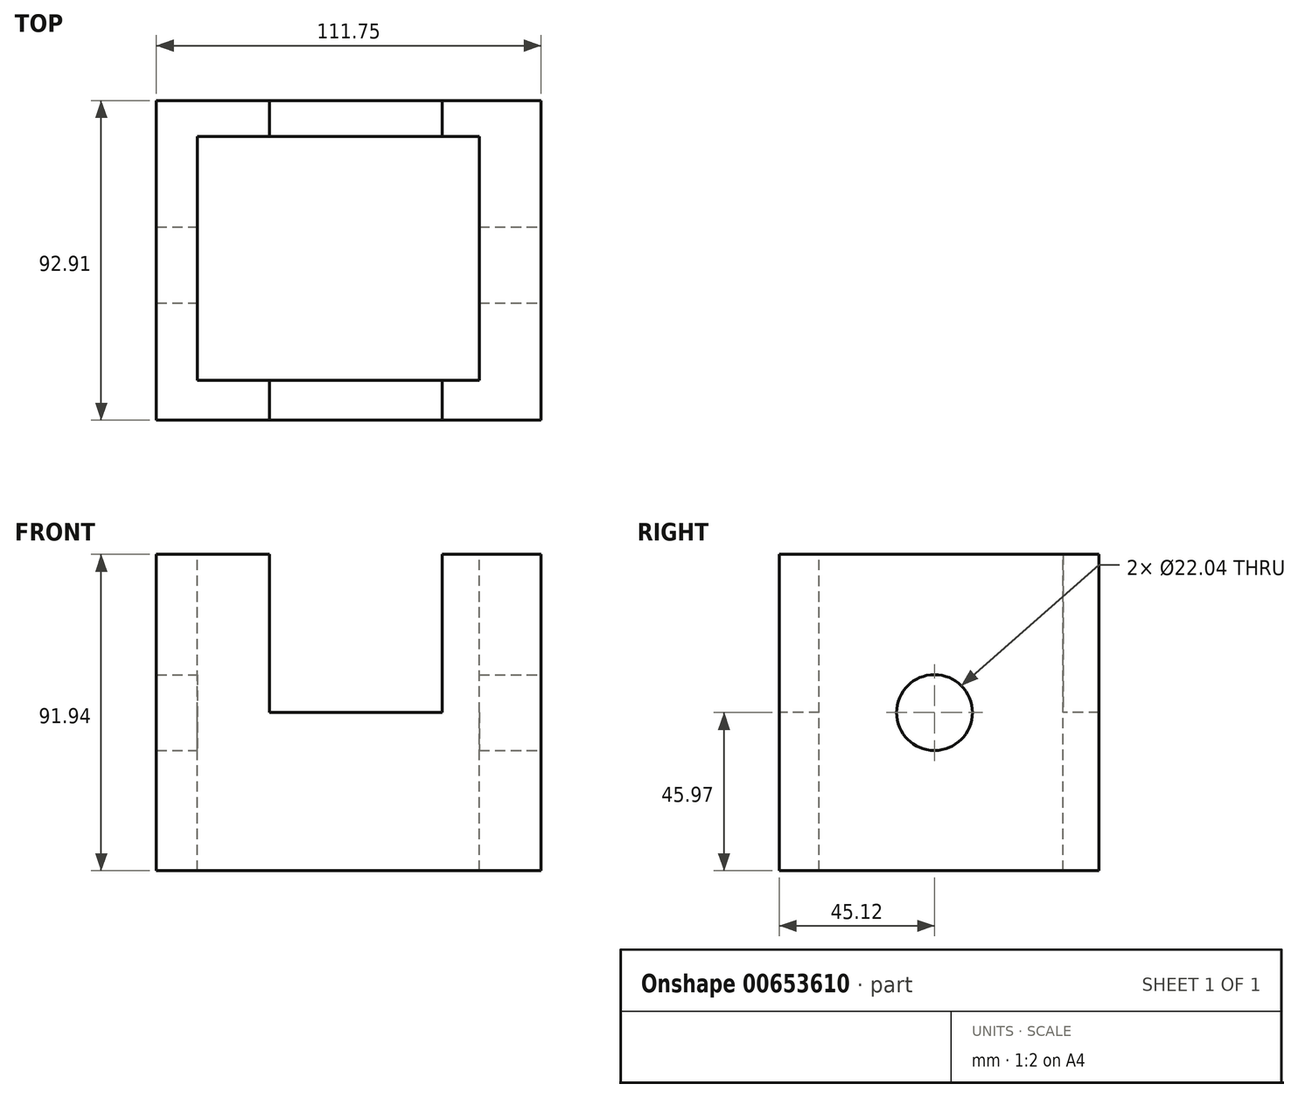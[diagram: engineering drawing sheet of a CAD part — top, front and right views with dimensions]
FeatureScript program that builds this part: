
annotation { "Feature Type Name" : "Feature", "Feature Type Description" : "" }
export const myFeature = defineFeature(function(context is Context, id is Id, definition is map)
    precondition{}
    {
        {
            var Q0;
            Q0=qCreatedBy(makeId("Top.planeOp"),FACE);
            var sketch = newSketch(context, id + "F0", { "sketchPlane" : qUnion([Q0])});
            skLineSegment(sketch, "E0", {"start": v(-56.34, 47.8) * mm, "end": v(-56.34, -45.12) * mm});
            skLineSegment(sketch, "E1", {"start": v(-56.34, -45.12) * mm, "end": v(55.41, -45.12) * mm});
            skLineSegment(sketch, "E2", {"start": v(55.41, -45.12) * mm, "end": v(55.41, 47.8) * mm});
            skLineSegment(sketch, "E3", {"start": v(55.41, 47.8) * mm, "end": v(-56.34, 47.8) * mm});
            skSolve(sketch);
        }
        {
            var Q0;
            Q0=makeQuery(id+"F0.imprint","IMPRINT",FACE,{"disambiguationData":[TD([[makeQuery(id+"F0.imprint","IMPRINT",EDGE,{"derivedFrom":sQuery(id+"F0.wireOp",EDGE,"E0")}),1.0]])]});
            extrude(context, id + "F1", {"entities" : qUnion([Q0]), "endBound" : BoundingType.SYMMETRIC, "depth" : 91.95 * mm, "offsetDistance" : 25.4 * mm});
        }
        {
            var Q0;
            Q0=makeQuery(id+"F1.opExtrude","CAP_FACE",FACE,{"disambiguationData":[OSD([sQuery(id+"F0.wireOp",EDGE,"E0"),sQuery(id+"F0.wireOp",EDGE,"E1"),sQuery(id+"F0.wireOp",EDGE,"E2"),sQuery(id+"F0.wireOp",EDGE,"E3")])],"isStart":false});
            var sketch = newSketch(context, id + "F2", { "sketchPlane" : qUnion([Q0])});
            skLineSegment(sketch, "E4", {"start": v(-44.43, 37.4) * mm, "end": v(37.4, 37.4) * mm});
            skLineSegment(sketch, "E5", {"start": v(37.4, 37.4) * mm, "end": v(37.4, -33.47) * mm});
            skLineSegment(sketch, "E6", {"start": v(37.4, -33.47) * mm, "end": v(-44.43, -33.47) * mm});
            skLineSegment(sketch, "E7", {"start": v(-44.43, -33.47) * mm, "end": v(-44.43, 37.4) * mm});
            skSolve(sketch);
        }
        {
            var Q0;
            Q0=makeQuery(id+"F2.imprint","IMPRINT",FACE,{"disambiguationData":[TD([[makeQuery(id+"F2.imprint","IMPRINT",EDGE,{"derivedFrom":sQuery(id+"F2.wireOp",EDGE,"E4")}),-1.0]])]});
            extrude(context, id + "F3", {"entities" : qUnion([Q0]), "operationType" : NewBodyOperationType.REMOVE, "endBound" : BoundingType.SYMMETRIC, "oppositeDirection" : true, "depth" : 219.46 * mm, "offsetDistance" : 25.4 * mm});
        }
        {
            var Q0;
            Q0=makeQuery(id+"F1.opExtrude","SWEPT_FACE",FACE,{"disambiguationData":[OSD([sQuery(id+"F0.wireOp",EDGE,"E2")])]});
            var sketch = newSketch(context, id + "F4", { "sketchPlane" : qUnion([Q0])});
            skCircle(sketch, "E8", {"center": v(0, 0) * mm, "radius": 11.02 * mm});
            skSolve(sketch);
        }
        {
            var Q0;
            Q0=makeQuery(id+"F4.imprint","IMPRINT",FACE,{"disambiguationData":[TD([[makeQuery(id+"F4.imprint","IMPRINT",EDGE,{"derivedFrom":sQuery(id+"F4.wireOp",EDGE,"E8")}),1.0]])]});
            extrude(context, id + "F5", {"entities" : qUnion([Q0]), "operationType" : NewBodyOperationType.REMOVE, "oppositeDirection" : true, "depth" : 176.02 * mm, "offsetDistance" : 25.4 * mm});
        }
        {
            var Q0;
            Q0=makeQuery(id+"F1.opExtrude","SWEPT_FACE",FACE,{"disambiguationData":[OSD([sQuery(id+"F0.wireOp",EDGE,"E1")])]});
            var sketch = newSketch(context, id + "F6", { "sketchPlane" : qUnion([Q0])});
            skLineSegment(sketch, "E9", {"start": v(-23.52, 45.97) * mm, "end": v(-23.52, 0) * mm});
            skLineSegment(sketch, "E10", {"start": v(-23.52, 0) * mm, "end": v(26.67, 0) * mm});
            skLineSegment(sketch, "E11", {"start": v(26.67, 0) * mm, "end": v(26.67, 45.97) * mm});
            skLineSegment(sketch, "E12", {"start": v(26.67, 45.97) * mm, "end": v(-23.52, 45.97) * mm});
            skSolve(sketch);
        }
        {
            var Q0;
            Q0=makeQuery(id+"F6.imprint","IMPRINT",FACE,{"disambiguationData":[TD([[makeQuery(id+"F6.imprint","IMPRINT",EDGE,{"derivedFrom":sQuery(id+"F6.wireOp",EDGE,"E9")}),1.0]])]});
            extrude(context, id + "F7", {"entities" : qUnion([Q0]), "operationType" : NewBodyOperationType.REMOVE, "oppositeDirection" : true, "depth" : 118.36 * mm, "offsetDistance" : 25.4 * mm});
        }
    });
